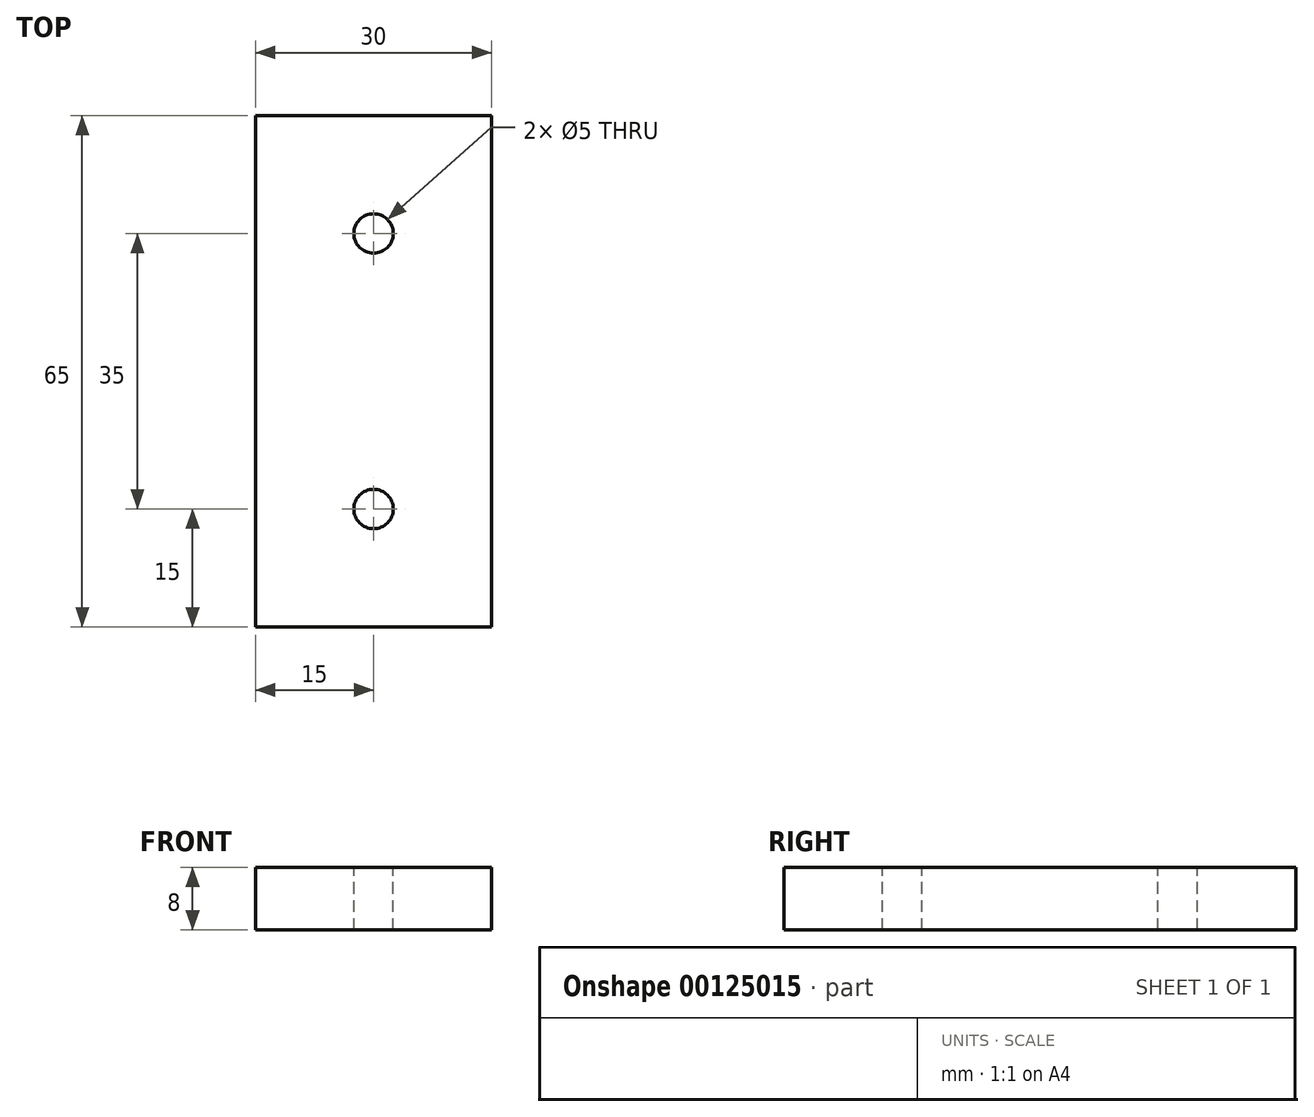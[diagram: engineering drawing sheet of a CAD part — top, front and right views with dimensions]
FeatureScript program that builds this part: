
annotation { "Feature Type Name" : "Feature", "Feature Type Description" : "" }
export const myFeature = defineFeature(function(context is Context, id is Id, definition is map)
    precondition{}
    {
        {
            var Q0;
            Q0=qCreatedBy(makeId("Top.planeOp"),FACE);
            var sketch = newSketch(context, id + "F0", { "sketchPlane" : qUnion([Q0])});
            skLineSegment(sketch, "E0.bottom", {"start": v(15, -32.5) * mm, "end": v(-15, -32.5) * mm});
            skLineSegment(sketch, "E0.top", {"start": v(15, 32.5) * mm, "end": v(-15, 32.5) * mm});
            skLineSegment(sketch, "E0.left", {"start": v(15, -32.5) * mm, "end": v(15, 32.5) * mm});
            skLineSegment(sketch, "E0.right", {"start": v(-15, -32.5) * mm, "end": v(-15, 32.5) * mm});
            skPoint(sketch, "E0.middle", {"position": v(0, 0) * mm});
            skSolve(sketch);
        }
        {
            var Q0;
            Q0 = qSketchRegion(id + "F0", true);
            extrude(context, id + "F1", {"entities" : qUnion([Q0]), "depth" : 8 * mm});
        }
        {
            var Q0;
            Q0=makeQuery(id+"F1.opExtrude","CAP_FACE",FACE,{"disambiguationData":[OSD([sQuery(id+"F0.wireOp",EDGE,"E0.bottom"),sQuery(id+"F0.wireOp",EDGE,"E0.top"),sQuery(id+"F0.wireOp",EDGE,"E0.left"),sQuery(id+"F0.wireOp",EDGE,"E0.right")])],"isStart":false});
            var sketch = newSketch(context, id + "F2", { "sketchPlane" : qUnion([Q0])});
            skLineSegment(sketch, "E1", {"start": v(0, 32.5) * mm, "end": v(0, -32.5) * mm, "construction": true});
            skLineSegment(sketch, "E2", {"start": v(15, 0) * mm, "end": v(-15, 0) * mm, "construction": true});
            skPoint(sketch, "E3", {"position": v(0, 17.5) * mm});
            skPoint(sketch, "E4", {"position": v(0, -17.5) * mm});
            skSolve(sketch);
        }
        {
            var Q0;
            Q0=sQuery(id+"F2.wireOp",VERTEX,"E4");
            var Q1;
            Q1=sQuery(id+"F2.wireOp",VERTEX,"E3");
            var Q2;
            Q2=makeQuery(id+"F1.opExtrude","SWEPT_BODY",BODY,{"disambiguationData":[OSD([sQuery(id+"F0.wireOp",EDGE,"E0.bottom"),sQuery(id+"F0.wireOp",EDGE,"E0.top"),sQuery(id+"F0.wireOp",EDGE,"E0.left"),sQuery(id+"F0.wireOp",EDGE,"E0.right")])]});
            hole(context, id + "F3", {"style" : HoleStyle.SIMPLE, "endStyle" : HoleEndStyle.THROUGH, "holeDiameter" : 5 * mm, "locations" : qUnion([Q0, Q1]), "scope" : qUnion([Q2]), "isTappedThrough" : true});
        }
    });
